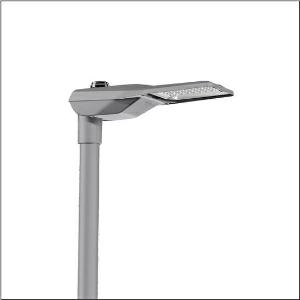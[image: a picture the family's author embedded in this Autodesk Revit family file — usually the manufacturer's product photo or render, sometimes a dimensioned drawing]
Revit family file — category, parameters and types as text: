
# Revit family: streetlight_sl_21_mini___st0_8a_5xe6c37n08hb_0120
name_source: partatom
category: Lighting Fixtures
units: mm (PartAtom-declared; Revit-internal decimal feet)

## family parameters
Cut with Voids When Loaded = No
Host = Face
Light Source = No
Part Type = Normal
Room Calculation Point = No
Round Connector Dimension = Use Diameter
Shared = No

## types (1)
- --- (1 x LED, 9040 lm, 66 W, 3000K)
    Apparent Load = 66 VA
    CIE Flux Codes = 38 75 97 100 100
    Color Rendering = 70
    Color Temperature = 3000K
    Default Elevation = 1800 mm
    Description = Streetlight SL 21 mini, mast luminaire, primary light control with lens, of PMMA, primary optical cover: cover, of toughened safety glass, transparent, light distribution: ST0.8a, light emission: direct distribution, primary light characteristic: asymmetric, installation type: side-entry, LED, 3G 1.5mm², High Power LED, rated luminous flux: 9.040lm, luminous efficacy: 137lm/W, light colour: 730, colour temperature: 3000K, control: overheat protection, pre-setting: linear dimming characteristic, constant luminous flux control, time-dependent luminous flux control, flexible luminous flux parameterisation, mains connection: 230..240V, AC, 50/60Hz, connection cable pre-assembled, cable length: 8,5m, wiring characteristics: H07RN-F, start of lifetime: 66W, end of service life: 69W, reduction: 30W, luminaire housing, of diecast aluminium (EN AC-44300), powder-coated, Siteco® metallic grey (DB 702S), corrosivity category C5 mid according to DIN EN ISO 12944, multi-level sealing system, sealing non-destructively replaceable, inclination adjustable: 0°, 5°, 10°, 15°, length: 628mm, width: 235mm, height: 110mm, spigot size: 42mm (side-entry), protection rating (complete): IP66, insulation class (complete): insulation class I (protective earthing), certification: CE, ENEC, ENEC+, VDE, impact resistance: IK09, permissible operating ambient temperature for outdoor applications: -40..+50°C, standard-compliant lighting for roads and squares, packaging unit: 1 piece

Light Distribution: ST0.8a
    Height = 110 mm
    Lamp = 1 x LED
    Lamp Light Flux = 9040 lm
    Lamp Power = 66 W
    Lamp count = 1
    Length = 625 mm
    Luminous efficacy = 137 lm/W
    Manufacturer = Siteco
    ModVariant = No
    Model = 5XE6C37N08HB
    Number of Poles = 1
    OnlyDefault = Yes
    Power Factor = 1
    Product Name = Streetlight SL 21 mini | ST0.8a
    Product group = mast luminaire | pylon top
    ProductGroupID = 6100
    Protection Class = Protection class I
    Protection Degree = IP 66
    RLX_Detail_Level = 1
    RLX_Emergency_Light_Flux = 0 lm
    RLX_Emergency_Type = 0
    RLX_Emergency_Type_DB = No
    RlxData = <blob elided: 93081 chars, md5=c199fd56>
    Socket = socket
    Standby Power = 0 W
    System Light Flux = 9040 lm
    System Power = 66 W
    Type Comments = factory setting: luminous flux: 100 % | dim-lin: 254 | 670 mA
    Type Image = l_1294379.jpg
    URL = http://relux.com
    VarID = @adj_104029
    Voltage = 0 V
    Weight = 0.00 kg
    Width = 234 mm

## geometry (parser evidence)
native form markers: Blend x4, Sweep x12
no freeform markers — native parametric forms only
